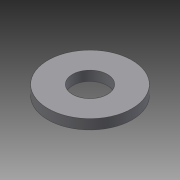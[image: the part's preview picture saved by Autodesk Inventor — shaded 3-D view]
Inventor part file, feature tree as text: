
AUTODESK INVENTOR PART (.ipt)
format: ipt  version: 2018 (Build 220112000, 112)  size: 103,424 bytes
history: native  units: mm
features: extrude x2, sketch x2, other x1, pattern_circular x1, chamfer x1
ambient origin geometry x8: Origin, YZ Plane, XZ Plane, XY Plane, X Axis, Y Axis, Z Axis, Center Point
bodies: Body1 (feature_tree)
feature tree (7):
  other  "ソリッド1"
  extrude  "押し出し1"  Depth=40.7mm
  extrude  "押し出し2"  Depth=17.0mm
  pattern_circular  "円形状パターン1"  [2 undecoded]
  chamfer  "面取り1"  Distance=15.0mm
  sketch  "スケッチ1"
  sketch  "スケッチ2"
note: 2 required parameter values undecoded (feature->parameter linkage not recoverable at this tier; creation-order binding heuristic only, values carry confidence <= 0.55)
